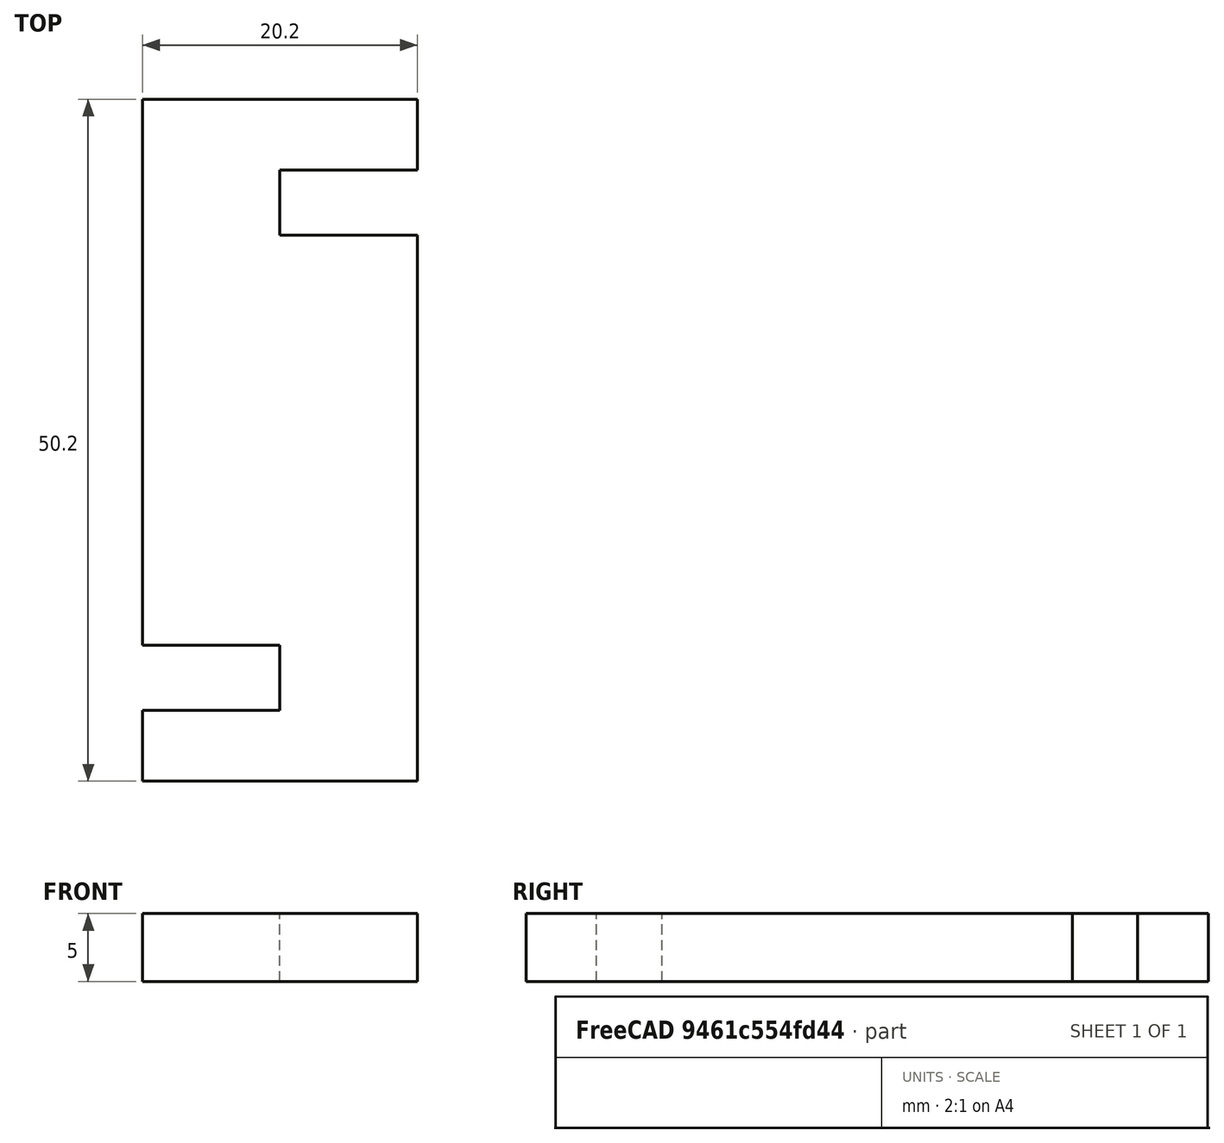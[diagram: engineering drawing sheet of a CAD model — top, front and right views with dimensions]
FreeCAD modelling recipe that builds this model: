
FCSTD DOCUMENT  (FreeCAD 0.16R6707 (Git))
Label: BearingStopMK2
License: All rights reserved
LicenseURL: http://en.wikipedia.org/wiki/All_rights_reserved
objects: Sketcher::SketchObject×1, PartDesign::Pad×1
note: 3 computed .brp shape members not serialized (recipe doc carries the construction recipe); baked Part::Feature solids carry a one-line shape summary decoded from their .brp

FEATURE [Sketcher::SketchObject] Sketch012
  Placement = pos=(0,-5,100) rot=(0,0,1;0rad)
  sketch-geometry (12):
    g0: LineSegment StartX=-10.1 StartY=25.1 StartZ=0 EndX=10.1 EndY=25.1 EndZ=0
    g1: LineSegment StartX=10.1 StartY=25.1 StartZ=0 EndX=10.1 EndY=19.9 EndZ=0
    g2: LineSegment StartX=10.1 StartY=19.9 StartZ=0 EndX=0 EndY=19.9 EndZ=0
    g3: LineSegment StartX=0 StartY=19.9 StartZ=0 EndX=0 EndY=15.1 EndZ=0
    g4: LineSegment StartX=0 StartY=15.1 StartZ=0 EndX=10.1 EndY=15.1 EndZ=0
    g5: LineSegment StartX=10.1 StartY=15.1 StartZ=0 EndX=10.1 EndY=-25.1 EndZ=0
    g6: LineSegment StartX=10.1 StartY=-25.1 StartZ=0 EndX=-10.1 EndY=-25.1 EndZ=0
    g7: LineSegment StartX=-10.1 StartY=-25.1 StartZ=0 EndX=-10.1 EndY=-19.9 EndZ=0
    g8: LineSegment StartX=-10.1 StartY=-19.9 StartZ=0 EndX=0 EndY=-19.9 EndZ=0
    g9: LineSegment StartX=0 StartY=-19.9 StartZ=0 EndX=0 EndY=-15.1 EndZ=0
    g10: LineSegment StartX=0 StartY=-15.1 StartZ=0 EndX=-10.1 EndY=-15.1 EndZ=0
    g11: LineSegment StartX=-10.1 StartY=-15.1 StartZ=0 EndX=-10.1 EndY=25.1 EndZ=0
  constraints (34):
    c: Horizontal(g0)
    c: Coincident(g0,g1)
    c: Vertical(g1)
    c: Coincident(g1,g2)
    c: PointOnObject(g2,g-2)
    c: Horizontal(g2)
    c: Coincident(g2,g3)
    c: Vertical(g3)
    c: Coincident(g3,g4)
    c: Horizontal(g4)
    c: Coincident(g4,g5)
    c: Vertical(g5)
    c: Coincident(g5,g6)
    c: Horizontal(g6)
    c: Coincident(g6,g7)
    c: Vertical(g7)
    c: Coincident(g7,g8)
    c: Coincident(g8,g9)
    c: Vertical(g9)
    c: Coincident(g9,g10)
    c: Horizontal(g10)
    c: Coincident(g10,g11)
    c: Coincident(g11,g0)
    c: Vertical(g11)
    c: Horizontal(g8)
    c: Symmetric(g5,g0,g-1)
    c: Symmetric(g6,g5,g-2)
    c: Symmetric(g0,g0,g-2)
    c: Symmetric(g9,g3,g-1)
    c: Symmetric(g8,g2,g-1)
    c: DistanceY(g3) = 15.1
    c: DistanceY(g9,g9) = 4.8
    c: DistanceY(g7,g7) = 5.2
    c: DistanceX(g0,g0) = 20.2
FEATURE [PartDesign::Pad] Pad
  Length = 5
  Length2 = 100
  Placement = pos=(0,-5,100) rot=(0,0,1;0rad)
  Sketch = -> Sketch012
  Type = 0
